# Revit family: RS222K.100.x.245
name_source: partatom
category: Sanitärinstallationen
units: mm (PartAtom-declared; Revit-internal decimal feet)

## family parameters
Arbeitsebenenbasiert = Nein
Beim Laden mit Abzugskörper schneiden = Nein
Bemaßung runder Anschluss = Durchmesser verwenden
Gemeinsam genutzt = Nein
Immer vertikal = Ja
Raumberechnungspunkt = Nein
Teiletyp = Normal

## types (1)
- RS222K.100.x.245
    Anschlusswert DU L/s = 0
    Baugruppenkennzeichen = D2030300
    Hersteller = Resitec
    Klebeblech mit Epoxidgrundierung = Nein
    RS_AVol-H = 230 mm  [stored 0.754593 ft]
    RS_AVol-L = 140 mm  [stored 0.459318 ft]
    RS_AVol-T = 140 mm  [stored 0.459318 ft]
    RS_DN1 = 100 mm  [stored 0.328084 ft]
    RS_DN1d = 110 mm  [stored 0.360892 ft]
    RS_DN2 = 0 mm  [stored 0 ft]
    RS_DVol-L = 300 mm  [stored 0.984252 ft]
    RS_DVol-T = 300 mm  [stored 0.984252 ft]
    RS_Manufacture = Resitec
    RS_URL = https://resitec.ch
    RS_dia001 = 114 mm  [stored 0.374016 ft]
    RS_dia002 = 130 mm  [stored 0.426509 ft]
    RS_dim001 = 75 mm  [stored 0.246063 ft]
    RS_dim002 = 158 mm
    RS_dim003 = 80 mm  [stored 0.262467 ft]
    RS_s001 = 3 mm  [stored 0.00984252 ft]
    URL = https://www.resitec.ch
    Vorgabe-Ansicht = 0 mm  [stored 0 ft]

note: [stored X ft] marks values corroborated as IEEE doubles in the binary element streams (Revit-internal decimal feet)

## geometry (parser evidence)
native form markers: Blend x8
no freeform markers — native parametric forms only
